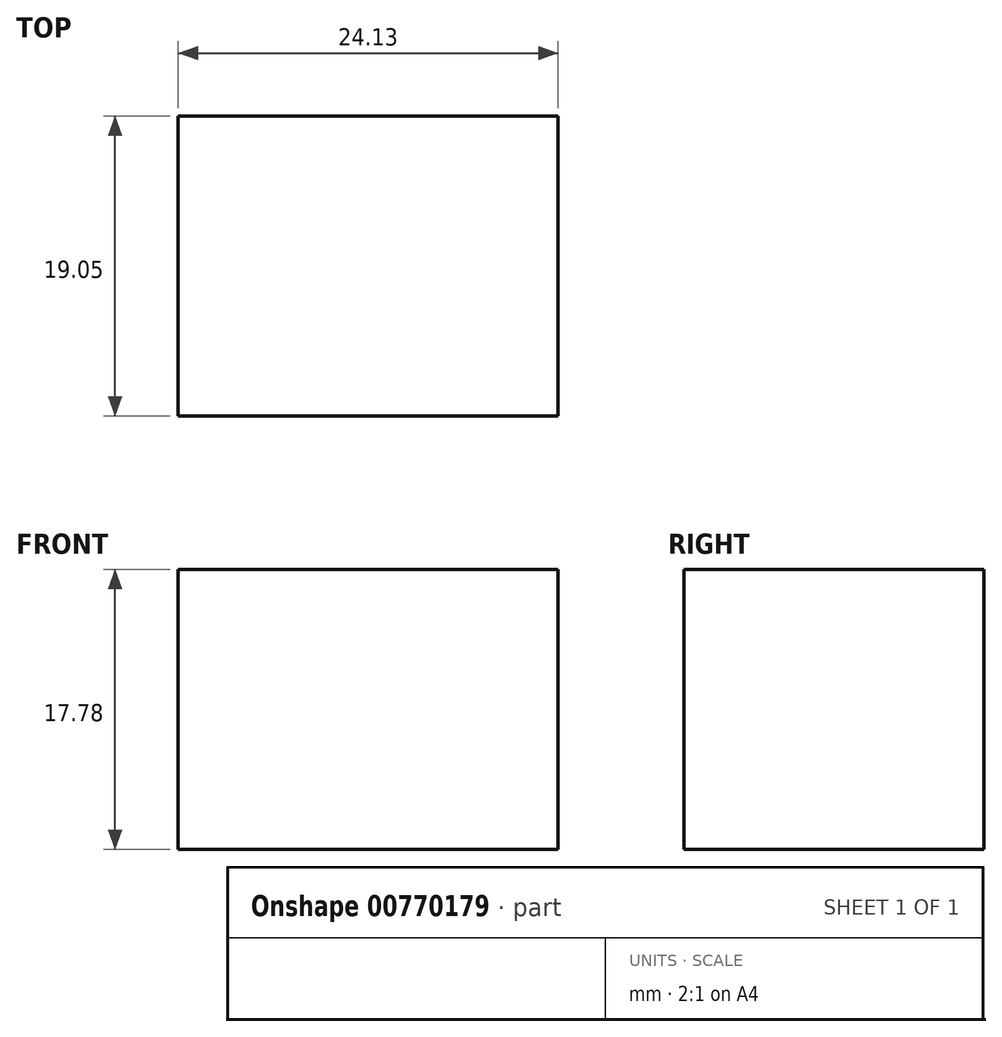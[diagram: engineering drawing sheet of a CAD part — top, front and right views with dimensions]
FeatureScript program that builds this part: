
annotation { "Feature Type Name" : "Feature", "Feature Type Description" : "" }
export const myFeature = defineFeature(function(context is Context, id is Id, definition is map)
    precondition{}
    {
        {
            var Q0;
            Q0=qCreatedBy(makeId("Right.planeOp"),FACE);
            var sketch = newSketch(context, id + "F0", { "sketchPlane" : qUnion([Q0])});
            skLineSegment(sketch, "E0.bottom", {"start": v(-19.05, 18.43) * mm, "end": v(0, 18.43) * mm});
            skLineSegment(sketch, "E0.top", {"start": v(-19.05, 36.21) * mm, "end": v(0, 36.21) * mm});
            skLineSegment(sketch, "E0.left", {"start": v(-19.05, 18.43) * mm, "end": v(-19.05, 36.21) * mm});
            skLineSegment(sketch, "E0.right", {"start": v(0, 18.43) * mm, "end": v(0, 36.21) * mm});
            skSolve(sketch);
        }
        {
            var Q0;
            Q0=makeQuery(id+"F0.imprint","IMPRINT",FACE,{"disambiguationData":[TD([[makeQuery(id+"F0.imprint","IMPRINT",EDGE,{"derivedFrom":sQuery(id+"F0.wireOp",EDGE,"E0.bottom")}),1.0]])]});
            extrude(context, id + "F1", {"entities" : qUnion([Q0]), "depth" : 24.13 * mm, "offsetDistance" : 25.4 * mm});
        }
    });
